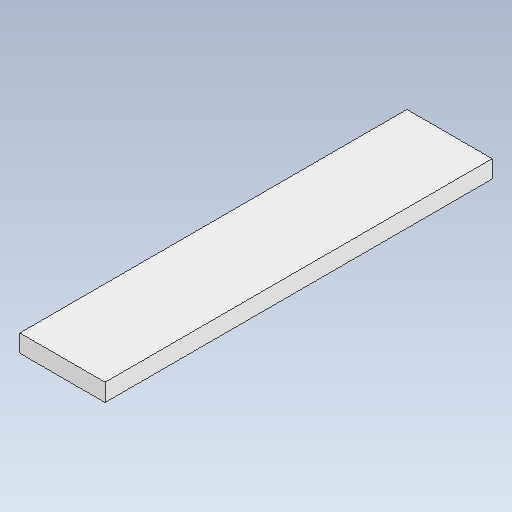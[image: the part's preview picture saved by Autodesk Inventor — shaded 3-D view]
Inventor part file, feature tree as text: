
AUTODESK INVENTOR PART (.ipt)
format: ipt  version: 2021 (Build 250183000, 183)  size: 91,136 bytes
history: native  units: mm
features: extrude x1, sketch x1
ambient origin geometry x8: Origin, YZ Plane, XZ Plane, XY Plane, X Axis, Y Axis, Z Axis, Center Point
bodies: Solid1 (feature_tree)
feature tree (2):
  extrude  "Extrusion1"  Depth=110.0mm
  sketch  "Sketch1"  dims[d0=24.226mm d1=110.0mm d2=5.0mm d3=0.0mm]
